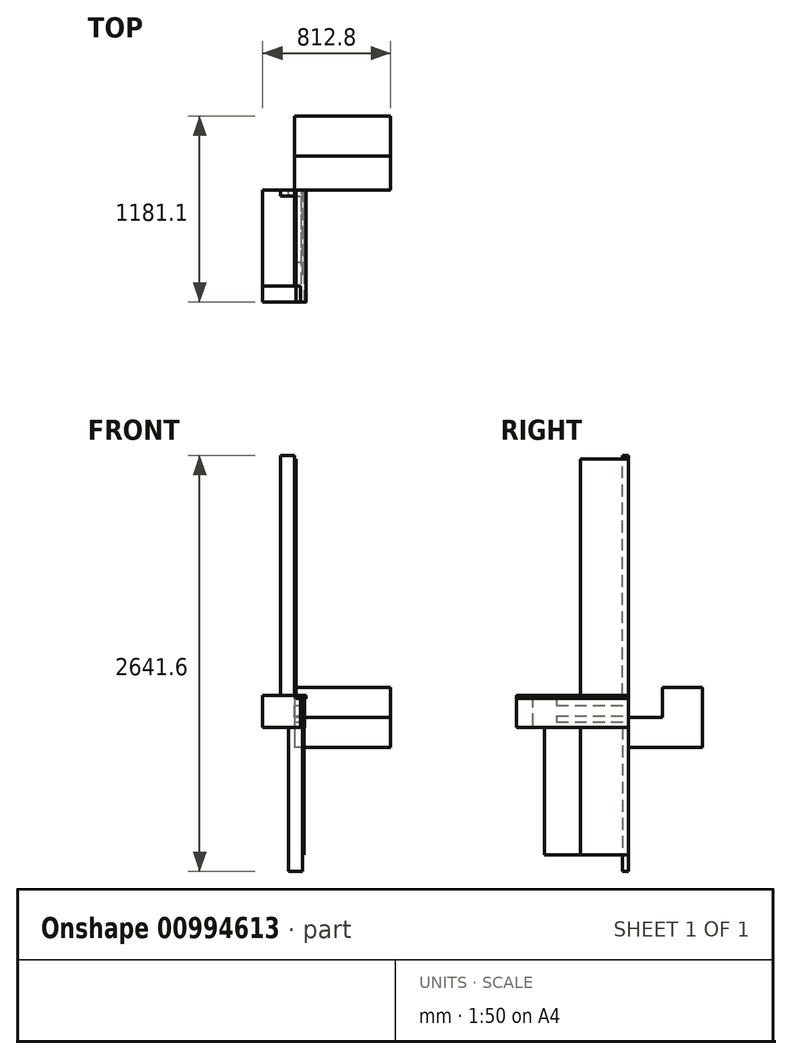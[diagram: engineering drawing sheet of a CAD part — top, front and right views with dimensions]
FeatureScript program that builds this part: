
annotation { "Feature Type Name" : "Feature", "Feature Type Description" : "" }
export const myFeature = defineFeature(function(context is Context, id is Id, definition is map)
    precondition{}
    {
        {
            var Q0;
            Q0=qCreatedBy(makeId("Front.planeOp"),FACE);
            var sketch = newSketch(context, id + "F0", { "sketchPlane" : qUnion([Q0])});
            skLineSegment(sketch, "E0", {"start": v(0, 1764.03) * mm, "end": v(0, 0) * mm, "construction": true});
            skLineSegment(sketch, "E1.bottom", {"start": v(0, 0) * mm, "end": v(-88.9, 0) * mm});
            skLineSegment(sketch, "E1.top", {"start": v(0, 1524) * mm, "end": v(-88.9, 1524) * mm});
            skLineSegment(sketch, "E1.left", {"start": v(0, 0) * mm, "end": v(0, 1524) * mm});
            skLineSegment(sketch, "E1.right", {"start": v(-88.9, 0) * mm, "end": v(-88.9, 1524) * mm});
            skLineSegment(sketch, "E2.bottom", {"start": v(0, 0) * mm, "end": v(-203.2, 0) * mm});
            skLineSegment(sketch, "E2.top", {"start": v(0, -203.2) * mm, "end": v(-203.2, -203.2) * mm});
            skLineSegment(sketch, "E2.left", {"start": v(0, 0) * mm, "end": v(0, -203.2) * mm});
            skLineSegment(sketch, "E2.right", {"start": v(-203.2, 0) * mm, "end": v(-203.2, -203.2) * mm});
            skLineSegment(sketch, "E3.bottom", {"start": v(-38.1, -203.2) * mm, "end": v(50.8, -203.2) * mm});
            skLineSegment(sketch, "E3.top", {"start": v(-38.1, -1117.6) * mm, "end": v(50.8, -1117.6) * mm});
            skLineSegment(sketch, "E3.left", {"start": v(-38.1, -203.2) * mm, "end": v(-38.1, -1117.6) * mm});
            skLineSegment(sketch, "E3.right", {"start": v(50.8, -203.2) * mm, "end": v(50.8, -1117.6) * mm});
            skLineSegment(sketch, "E4.bottom", {"start": v(50.8, -203.2) * mm, "end": v(60.32, -203.2) * mm});
            skLineSegment(sketch, "E4.top", {"start": v(50.8, -1014.14) * mm, "end": v(60.33, -1014.14) * mm});
            skLineSegment(sketch, "E4.left", {"start": v(50.8, -203.2) * mm, "end": v(50.8, -1014.14) * mm});
            skLineSegment(sketch, "E4.right", {"start": v(60.32, -203.2) * mm, "end": v(60.33, -1014.14) * mm});
            skLineSegment(sketch, "E5.bottom", {"start": v(0, 1502.1) * mm, "end": v(9.52, 1502.1) * mm});
            skLineSegment(sketch, "E5.top", {"start": v(0, -15.38) * mm, "end": v(9.53, -15.38) * mm});
            skLineSegment(sketch, "E5.left", {"start": v(0, 1502.1) * mm, "end": v(0, -15.38) * mm});
            skLineSegment(sketch, "E5.right", {"start": v(9.52, 1502.1) * mm, "end": v(9.52, -15.38) * mm});
            skLineSegment(sketch, "E6.bottom", {"start": v(44.45, -19.05) * mm, "end": v(63.5, -19.05) * mm});
            skLineSegment(sketch, "E6.top", {"start": v(44.45, -203.2) * mm, "end": v(63.5, -203.2) * mm});
            skLineSegment(sketch, "E6.left", {"start": v(44.45, -19.05) * mm, "end": v(44.45, -203.2) * mm});
            skLineSegment(sketch, "E6.right", {"start": v(63.5, -19.05) * mm, "end": v(63.5, -203.2) * mm});
            skLineSegment(sketch, "E7.bottom", {"start": v(9.52, 0) * mm, "end": v(73.02, 0) * mm});
            skLineSegment(sketch, "E7.top", {"start": v(9.52, -19.05) * mm, "end": v(63.5, -19.05) * mm});
            skLineSegment(sketch, "E7.left", {"start": v(9.52, 0) * mm, "end": v(9.52, -19.05) * mm});
            skLineSegment(sketch, "E8.bottom", {"start": v(0, -130.9) * mm, "end": v(44.45, -130.9) * mm});
            skLineSegment(sketch, "E8.top", {"start": v(0, -169) * mm, "end": v(44.45, -169) * mm});
            skLineSegment(sketch, "E8.left", {"start": v(0, -130.9) * mm, "end": v(0, -169) * mm});
            skLineSegment(sketch, "E8.right", {"start": v(44.45, -130.9) * mm, "end": v(44.45, -169) * mm});
            skLineSegment(sketch, "E9.bottom", {"start": v(0, -19.05) * mm, "end": v(44.45, -19.05) * mm});
            skLineSegment(sketch, "E9.top", {"start": v(0, -63.5) * mm, "end": v(44.45, -63.5) * mm});
            skLineSegment(sketch, "E9.left", {"start": v(0, -19.05) * mm, "end": v(0, -63.5) * mm});
            skLineSegment(sketch, "E9.right", {"start": v(44.45, -19.05) * mm, "end": v(44.45, -63.5) * mm});
            skLineSegment(sketch, "E10", {"start": v(73.02, 0) * mm, "end": v(73.02, -19.05) * mm});
            skLineSegment(sketch, "E11", {"start": v(73.02, -19.05) * mm, "end": v(63.5, -19.05) * mm});
            skSolve(sketch);
        }
        {
            var Q0;
            Q0=makeQuery(id+"F0.imprint","IMPRINT",FACE,{"disambiguationData":[TD([[makeQuery(id+"F0.imprint","IMPRINT",EDGE,{"derivedFrom":sQuery(id+"F0.wireOp",EDGE,"E1.top")}),1.0]])]});
            var Q1;
            {var subQ1=sQuery(id+"F0.wireOp",EDGE,"E3.top");Q1=makeQuery(id+"F0.imprint","IMPRINT",FACE,{"disambiguationData":[TD([[makeQuery(id+"F0.imprint","IMPRINT",EDGE,{"derivedFrom":subQ1}),1.0]])]});}
            extrude(context, id + "F1", {"entities" : qUnion([Q0, Q1]), "depth" : 38.1 * mm, "offsetDistance" : 25.4 * mm});
        }
        {
            var Q0;
            {var subQ3=sQuery(id+"F0.wireOp",EDGE,"E5.bottom");Q0=makeQuery(id+"F0.imprint","IMPRINT",FACE,{"disambiguationData":[TD([[makeQuery(id+"F0.imprint","IMPRINT",EDGE,{"derivedFrom":subQ3}),-1.0]])]});}
            var Q1;
            Q1=makeQuery(id+"F0.imprint","IMPRINT",FACE,{"disambiguationData":[TD([[makeQuery(id+"F0.imprint","IMPRINT",EDGE,{"derivedFrom":sQuery(id+"F0.wireOp",EDGE,"E4.bottom")}),-1.0]])]});
            extrude(context, id + "F2", {"entities" : qUnion([Q0, Q1]), "depth" : 304.8 * mm, "offsetDistance" : 25.4 * mm});
        }
        {
            var Q0;
            {var subQ6=sQuery(id+"F0.wireOp",EDGE,"E2.top");Q0=makeQuery(id+"F0.imprint","IMPRINT",FACE,{"disambiguationData":[TD([[makeQuery(id+"F0.imprint","IMPRINT",EDGE,{"derivedFrom":subQ6}),-1.0]])]});}
            extrude(context, id + "F3", {"entities" : qUnion([Q0]), "depth" : 609.6 * mm, "offsetDistance" : 25.4 * mm});
        }
        {
            var Q0;
            Q0=makeQuery(id+"F0.imprint","IMPRINT",FACE,{"disambiguationData":[TD([[makeQuery(id+"F0.imprint","IMPRINT",EDGE,{"derivedFrom":sQuery(id+"F0.wireOp",EDGE,"E9.top")}),1.0]])]});
            var Q1;
            Q1=makeQuery(id+"F0.imprint","IMPRINT",FACE,{"disambiguationData":[TD([[makeQuery(id+"F0.imprint","IMPRINT",EDGE,{"derivedFrom":sQuery(id+"F0.wireOp",EDGE,"E8.bottom")}),-1.0]])]});
            extrude(context, id + "F4", {"entities" : qUnion([Q0, Q1]), "depth" : 457.2 * mm, "offsetDistance" : 25.4 * mm});
        }
        {
            var Q0;
            Q0=makeQuery(id+"F3.opExtrude","SWEPT_FACE",FACE,{"disambiguationData":[OSD([sQuery(id+"F0.wireOp",EDGE,"E2.left"),sQuery(id+"F0.wireOp",EDGE,"E5.left"),sQuery(id+"F0.wireOp",EDGE,"E8.left"),sQuery(id+"F0.wireOp",EDGE,"E9.left")])]});
            var sketch = newSketch(context, id + "F5", { "sketchPlane" : qUnion([Q0])});
            skLineSegment(sketch, "E12.bottom", {"start": v(-609.6, 0) * mm, "end": v(-711.2, 0) * mm});
            skLineSegment(sketch, "E12.top", {"start": v(-609.6, -203.2) * mm, "end": v(-711.2, -203.2) * mm});
            skLineSegment(sketch, "E12.left", {"start": v(-609.6, 0) * mm, "end": v(-609.6, -203.2) * mm});
            skLineSegment(sketch, "E12.right", {"start": v(-711.2, 0) * mm, "end": v(-711.2, -203.2) * mm});
            skSolve(sketch);
        }
        {
            var Q0;
            Q0 = qSketchRegion(id + "F5", true);
            extrude(context, id + "F6", {"entities" : qUnion([Q0]), "depth" : 38.1 * mm, "offsetDistance" : 25.4 * mm, "hasSecondDirection" : true, "secondDirectionOppositeDirection" : true, "secondDirectionDepth" : 203.2 * mm});
        }
        {
            var Q0;
            {var subQ6=sQuery(id+"F0.wireOp",EDGE,"E6.right");Q0=makeQuery(id+"F0.imprint","IMPRINT",FACE,{"disambiguationData":[TD([[makeQuery(id+"F0.imprint","IMPRINT",EDGE,{"derivedFrom":subQ6}),-1.0]])]});}
            var Q1;
            Q1=makeQuery(id+"F6.opExtrude","SWEPT_FACE",FACE,{"disambiguationData":[OSD([sQuery(id+"F5.wireOp",EDGE,"E12.right")])]});
            extrude(context, id + "F7", {"entities" : qUnion([Q0]), "endBound" : BoundingType.UP_TO_SURFACE, "depth" : 25.4 * mm, "endBoundEntityFace" : qUnion([Q1]), "offsetDistance" : 25.4 * mm});
        }
        {
            var Q0;
            {var subQ4=sQuery(id+"F0.wireOp",EDGE,"E7.bottom");Q0=makeQuery(id+"F0.imprint","IMPRINT",FACE,{"disambiguationData":[TD([[makeQuery(id+"F0.imprint","IMPRINT",EDGE,{"derivedFrom":subQ4}),-1.0]])]});}
            var Q1;
            Q1=makeQuery(id+"F6.opExtrude","SWEPT_FACE",FACE,{"disambiguationData":[OSD([sQuery(id+"F5.wireOp",EDGE,"E12.right")])]});
            extrude(context, id + "F8", {"entities" : qUnion([Q0]), "endBound" : BoundingType.UP_TO_SURFACE, "depth" : 25.4 * mm, "endBoundEntityFace" : qUnion([Q1]), "offsetDistance" : 25.4 * mm});
        }
        {
            var Q0;
            Q0=makeQuery(id+"F0.imprint","IMPRINT",FACE,{"disambiguationData":[TD([[makeQuery(id+"F0.imprint","IMPRINT",EDGE,{"derivedFrom":sQuery(id+"F0.wireOp",EDGE,"E4.top")}),1.0]])]});
            extrude(context, id + "F9", {"entities" : qUnion([Q0]), "depth" : 533.4 * mm, "offsetDistance" : 25.4 * mm});
        }
        {
            var Q0;
            Q0=qCreatedBy(makeId("Right.planeOp"),FACE);
            var sketch = newSketch(context, id + "F10", { "sketchPlane" : qUnion([Q0])});
            skLineSegment(sketch, "E13", {"start": v(0, -139.7) * mm, "end": v(215.9, -139.7) * mm});
            skLineSegment(sketch, "E14", {"start": v(215.9, -139.7) * mm, "end": v(215.9, 50.8) * mm});
            skLineSegment(sketch, "E15", {"start": v(215.9, 50.8) * mm, "end": v(469.9, 50.8) * mm});
            skLineSegment(sketch, "E16", {"start": v(469.9, 50.8) * mm, "end": v(469.9, -330.2) * mm});
            skLineSegment(sketch, "E17", {"start": v(469.9, -330.2) * mm, "end": v(0, -330.2) * mm});
            skLineSegment(sketch, "E18", {"start": v(0, -139.7) * mm, "end": v(0, -330.2) * mm});
            skSolve(sketch);
        }
        {
            var Q0;
            Q0 = qSketchRegion(id + "F10", true);
            extrude(context, id + "F11", {"entities" : qUnion([Q0]), "depth" : 609.6 * mm, "offsetDistance" : 25.4 * mm});
        }
        {
            var Q0;
            Q0=makeQuery(id+"F8.opExtrude","SWEPT_EDGE",EDGE,{"disambiguationData":[OSD([sQuery(id+"F0.wireOp",EDGE,"E7.bottom"),sQuery(id+"F0.wireOp",EDGE,"E10")])]});
            fillet(context, id + "F12", {"entities" : qUnion([Q0]), "radius" : 6.35 * mm, "tangentPropagation" : true, "allowEdgeOverflow" : false});
        }
        {
            var Q0;
            Q0=makeQuery(id+"F8.opExtrude","SWEPT_EDGE",EDGE,{"disambiguationData":[OSD([sQuery(id+"F0.wireOp",EDGE,"E10"),sQuery(id+"F0.wireOp",EDGE,"E11")])]});
            fillet(context, id + "F13", {"entities" : qUnion([Q0]), "radius" : 3.17 * mm, "tangentPropagation" : true, "allowEdgeOverflow" : false});
        }
    });
